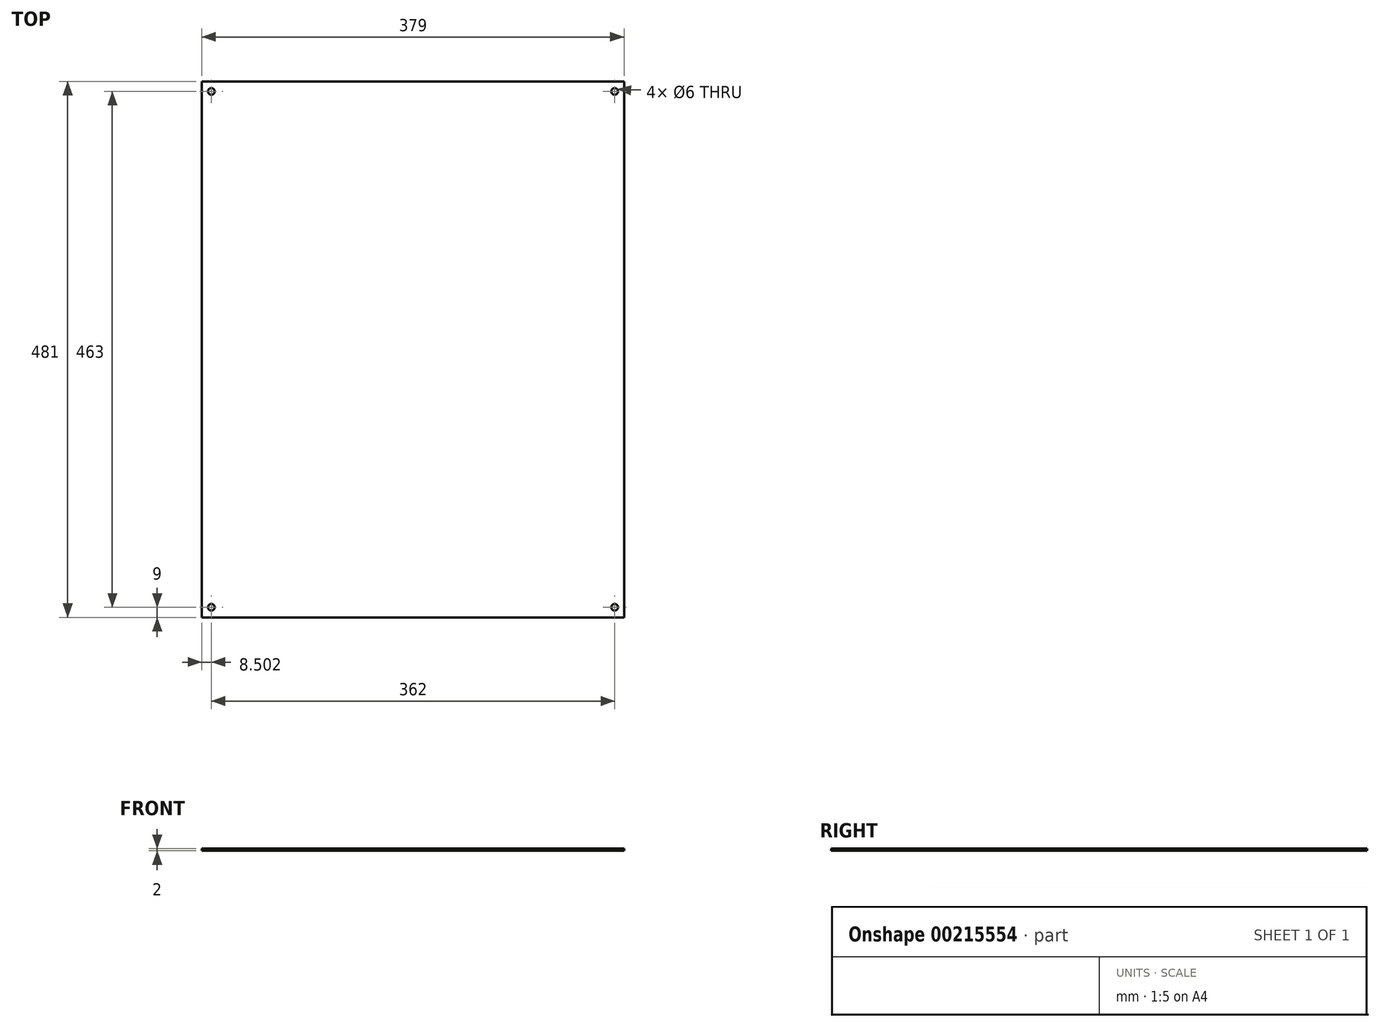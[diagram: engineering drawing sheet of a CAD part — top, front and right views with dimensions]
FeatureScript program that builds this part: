
annotation { "Feature Type Name" : "Feature", "Feature Type Description" : "" }
export const myFeature = defineFeature(function(context is Context, id is Id, definition is map)
    precondition{}
    {
        {
            var Q0;
            Q0=qCreatedBy(makeId("Top.planeOp"),FACE);
            var sketch = newSketch(context, id + "F0", { "sketchPlane" : qUnion([Q0])});
            skLineSegment(sketch, "E0.bottom", {"start": v(4.16, 0) * mm, "end": v(383.16, 0) * mm});
            skLineSegment(sketch, "E0.top", {"start": v(4.16, 481) * mm, "end": v(383.16, 481) * mm});
            skLineSegment(sketch, "E0.left", {"start": v(4.16, 0) * mm, "end": v(4.16, 481) * mm});
            skLineSegment(sketch, "E0.right", {"start": v(383.16, 0) * mm, "end": v(383.16, 481) * mm});
            skCircle(sketch, "E1", {"center": v(12.66, 9) * mm, "radius": 3 * mm});
            skCircle(sketch, "E2", {"center": v(12.66, 472) * mm, "radius": 3 * mm});
            skCircle(sketch, "E3", {"center": v(374.66, 472) * mm, "radius": 3 * mm});
            skCircle(sketch, "E4", {"center": v(374.66, 9) * mm, "radius": 3 * mm});
            skSolve(sketch);
        }
        {
            var Q0;
            Q0 = qSketchRegion(id + "F0", true);
            extrude(context, id + "F1", {"entities" : qUnion([Q0]), "depth" : 2 * mm});
        }
    });
